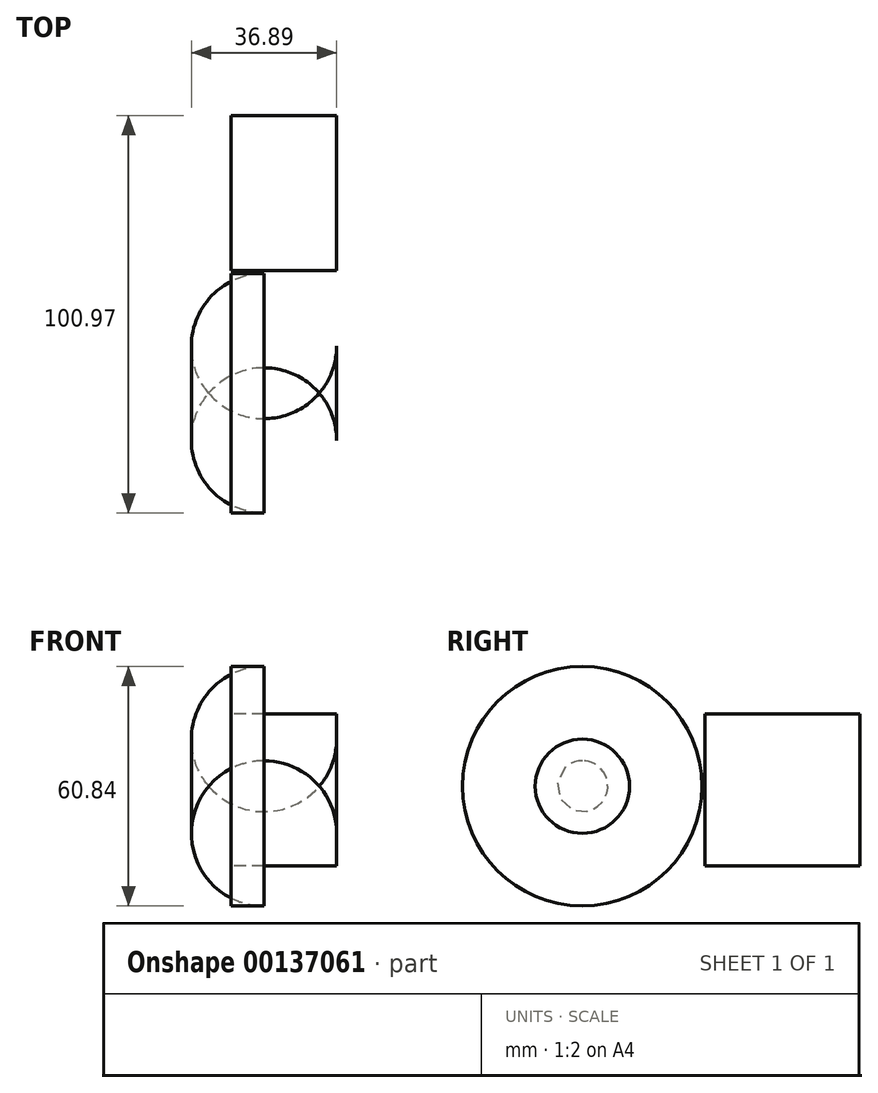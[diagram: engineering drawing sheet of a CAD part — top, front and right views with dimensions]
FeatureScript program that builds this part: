
annotation { "Feature Type Name" : "Feature", "Feature Type Description" : "" }
export const myFeature = defineFeature(function(context is Context, id is Id, definition is map)
    precondition{}
    {
        {
            var Q0;
            Q0=qCreatedBy(makeId("Right.planeOp"),FACE);
            var sketch = newSketch(context, id + "F0", { "sketchPlane" : qUnion([Q0])});
            skCircle(sketch, "E0", {"center": v(0, 0) * mm, "radius": 30.42 * mm});
            skLineSegment(sketch, "E1.bottom", {"start": v(70.55, 18.4) * mm, "end": v(31.13, 18.4) * mm});
            skLineSegment(sketch, "E1.top", {"start": v(70.55, -20.23) * mm, "end": v(31.13, -20.23) * mm});
            skLineSegment(sketch, "E1.left", {"start": v(70.55, 18.4) * mm, "end": v(70.55, -20.23) * mm});
            skLineSegment(sketch, "E1.right", {"start": v(31.13, 18.4) * mm, "end": v(31.13, -20.23) * mm});
            skSolve(sketch);
        }
        {
            var Q0;
            Q0 = qSketchRegion(id + "F0", true);
            extrude(context, id + "F1", {"entities" : qUnion([Q0]), "depth" : 26.78 * mm});
        }
        {
            var Q0;
            Q0=makeQuery(id+"F1.opExtrude","CAP_FACE",FACE,{"disambiguationData":[OSD([sQuery(id+"F0.wireOp",EDGE,"E0")])],"isStart":false});
            fillet(context, id + "F2", {"entities" : qUnion([Q0]), "radius" : 18.45 * mm, "tangentPropagation" : true, "allowEdgeOverflow" : false});
        }
        {
            var Q0;
            Q0=sQuery(id+"F0.wireOp",EDGE,"E1.left");
            var Q1;
            Q1=sQuery(id+"F0.wireOp",EDGE,"E1.right");
            var Q2;
            Q2=sQuery(id+"F0.wireOp",EDGE,"E1.bottom");
            var Q3;
            Q3=sQuery(id+"F0.wireOp",EDGE,"E1.top");
            var Q4;
            Q4=sQuery(id+"F0.wireOp",EDGE,"E0");
            extrude(context, id + "F3", {"bodyType" : ToolBodyType.SURFACE, "surfaceEntities" : qUnion([Q0, Q1, Q2, Q3, Q4]), "depth" : 13.6 * mm});
        }
    });
